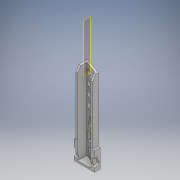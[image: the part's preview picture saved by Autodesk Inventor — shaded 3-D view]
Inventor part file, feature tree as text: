
AUTODESK INVENTOR PART (.ipt)
format: ipt  version: 2017 (Build 210142000, 142)  size: 238,592 bytes
history: native  units: mm
features: extrude x6, sketch x5, plane x1, thicken_offset x1, mirror x1, pattern_linear x1
ambient origin geometry x8: Origin, YZ Plane, XZ Plane, XY Plane, X Axis, Y Axis, Z Axis, Center Point
bodies: Solid1 (feature_tree)
feature tree (15):
  extrude  "Extrusion1"  Depth=9.0mm
  sketch  "Sketch2"  dims[d3=200.0mm d4=0.0mm d5=14.0mm]
  plane  "Work Plane1"
  thicken_offset  "Thicken1"
  extrude  "Extrusion6"  Depth=14.0mm
  mirror  "Mirror2"
  extrude  "Extrusion7"  Depth=14.0mm
  extrude  "Extrusion8"  Depth=20.0mm TaperAngle=15.0deg
  extrude  "Extrusion10"  Depth=30.0mm
  extrude  "Extrusion11"  Depth=27.0mm
  pattern_linear  "Rectangular Pattern1"  Spacing1=3.0mm  [1 undecoded]
  sketch  "Sketch1"  dims[d0=9.0mm d2=19.198622mm]
  sketch  "Sketch5"  dims[d6=14.0mm d9=72.0mm]
  sketch  "Sketch7"  dims[d10=20.0mm d12=15.0deg d14=20.0mm d16=15.0deg]
  sketch  "Sketch8"  dims[d19=4.0mm d26=30.0mm d29=-13.5mm d30=27.0mm d38=3.0mm d39=3.0mm d42=3.0mm d43=0.0mm d44=0.0mm d45=0.0mm d46=3.0mm d52=12.0mm d53=19.198622mm d57=2.0mm d58=3.0mm d59=0.0mm d60=8.0mm d77=10.0mm d78=105.256958mm d79=150.0deg d80=0.0mm d81=0.0mm d85=9.0mm d89=10.0mm d93=7.0mm d94=10.0mm d95=0.0mm d96=40.0mm d98=15.0mm]
note: 1 required parameter value undecoded (feature->parameter linkage not recoverable at this tier; creation-order binding heuristic only, values carry confidence <= 0.55)
